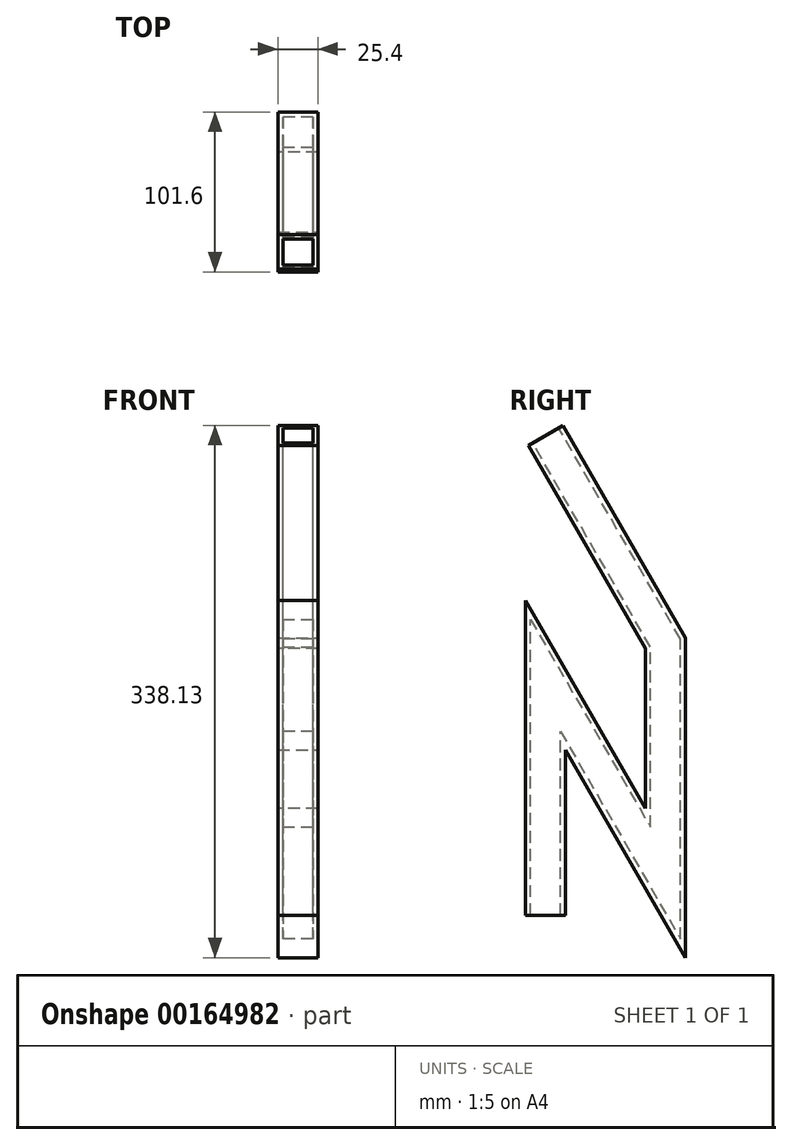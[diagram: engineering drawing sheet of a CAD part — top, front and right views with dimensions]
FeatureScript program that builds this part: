
annotation { "Feature Type Name" : "Feature", "Feature Type Description" : "" }
export const myFeature = defineFeature(function(context is Context, id is Id, definition is map)
    precondition{}
    {
        {
            var Q0;
            Q0=qCreatedBy(makeId("Top.planeOp"),FACE);
            var sketch = newSketch(context, id + "F0", { "sketchPlane" : qUnion([Q0])});
            skLineSegment(sketch, "E0.bottom", {"start": v(12.7, -12.7) * mm, "end": v(-12.7, -12.7) * mm});
            skLineSegment(sketch, "E0.top", {"start": v(12.7, 12.7) * mm, "end": v(-12.7, 12.7) * mm});
            skLineSegment(sketch, "E0.left", {"start": v(12.7, -12.7) * mm, "end": v(12.7, 12.7) * mm});
            skLineSegment(sketch, "E0.right", {"start": v(-12.7, -12.7) * mm, "end": v(-12.7, 12.7) * mm});
            skPoint(sketch, "E0.middle", {"position": v(0, 0) * mm});
            skLineSegment(sketch, "E1.bottom", {"start": v(-9.53, -9.53) * mm, "end": v(9.52, -9.53) * mm});
            skLineSegment(sketch, "E1.top", {"start": v(-9.53, 9.52) * mm, "end": v(9.52, 9.52) * mm});
            skLineSegment(sketch, "E1.left", {"start": v(-9.53, -9.52) * mm, "end": v(-9.53, 9.52) * mm});
            skLineSegment(sketch, "E1.right", {"start": v(9.52, -9.52) * mm, "end": v(9.52, 9.52) * mm});
            skSolve(sketch);
        }
        {
            var Q0;
            Q0=qCreatedBy(makeId("Right.planeOp"),FACE);
            var sketch = newSketch(context, id + "F1", { "sketchPlane" : qUnion([Q0])});
            skLineSegment(sketch, "E2", {"start": v(0, 0) * mm, "end": v(0, 152.4) * mm});
            skLineSegment(sketch, "E3", {"start": v(0, 152.4) * mm, "end": v(76.2, 20.42) * mm});
            skLineSegment(sketch, "E4", {"start": v(76.2, 20.42) * mm, "end": v(76.2, 172.82) * mm});
            skLineSegment(sketch, "E5", {"start": v(76.2, 172.82) * mm, "end": v(0, 304.8) * mm});
            skLineSegment(sketch, "E6", {"start": v(0, 304.8) * mm, "end": v(0, 152.4) * mm, "construction": true});
            skSolve(sketch);
        }
        {
            var Q0;
            Q0=makeQuery(id+"F0.imprint","IMPRINT",FACE,{"disambiguationData":[TD([[makeQuery(id+"F0.imprint","IMPRINT",EDGE,{"derivedFrom":sQuery(id+"F0.wireOp",EDGE,"E0.bottom")}),-1.0]])]});
            var Q1;
            Q1=sQuery(id+"F1.wireOp",EDGE,"E2");
            var Q2;
            Q2=sQuery(id+"F1.wireOp",EDGE,"E3");
            var Q3;
            Q3=sQuery(id+"F1.wireOp",EDGE,"E4");
            var Q4;
            Q4=sQuery(id+"F1.wireOp",EDGE,"E5");
            sweep(context, id + "F2", {"profiles" : qUnion([Q0]), "path" : qUnion([Q1, Q2, Q3, Q4])});
        }
    });
